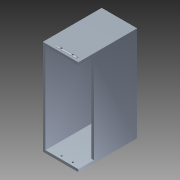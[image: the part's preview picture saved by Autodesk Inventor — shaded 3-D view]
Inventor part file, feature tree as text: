
AUTODESK INVENTOR PART (.ipt)
format: ipt  version: 2015 (Build 190159000, 159)  size: 220,160 bytes
history: native  units: in
note: dims shown in document units (in); Inventor stores cm internally (conversion verified against a paired STEP export)
features: sketch x3, extrude x2, direct_edit x2, projected_geometry x2, move_body x2, imported_body x1
ambient origin geometry x8: Origin, YZ Plane, XZ Plane, XY Plane, X Axis, Y Axis, Z Axis, Center Point
bodies: Solid1 (feature_tree)
feature tree (12):
  imported_body  "Base1"
  sketch  "Sketch2"  dims[d0=30.0in d1=0.0in d2=30.0in d3=0.0in]
  extrude  "Extrusion1"  Depth=30.0in TaperAngle=0.0deg
  extrude  "Extrusion2"  Depth=30.0in TaperAngle=0.0deg
  direct_edit  "Direct Edit3"
  direct_edit  "Direct Edit4"
  sketch  "Sketch3"  dims[d10=0.0in d11=30.0in d12=0.0in d13=0.0in d14=30.0in d15=0.0in]
  projected_geometry  "Projected Loop1"
  sketch  "Sketch4"
  projected_geometry  "Projected Loop2"
  move_body  "Move3"
  move_body  "Move4"
